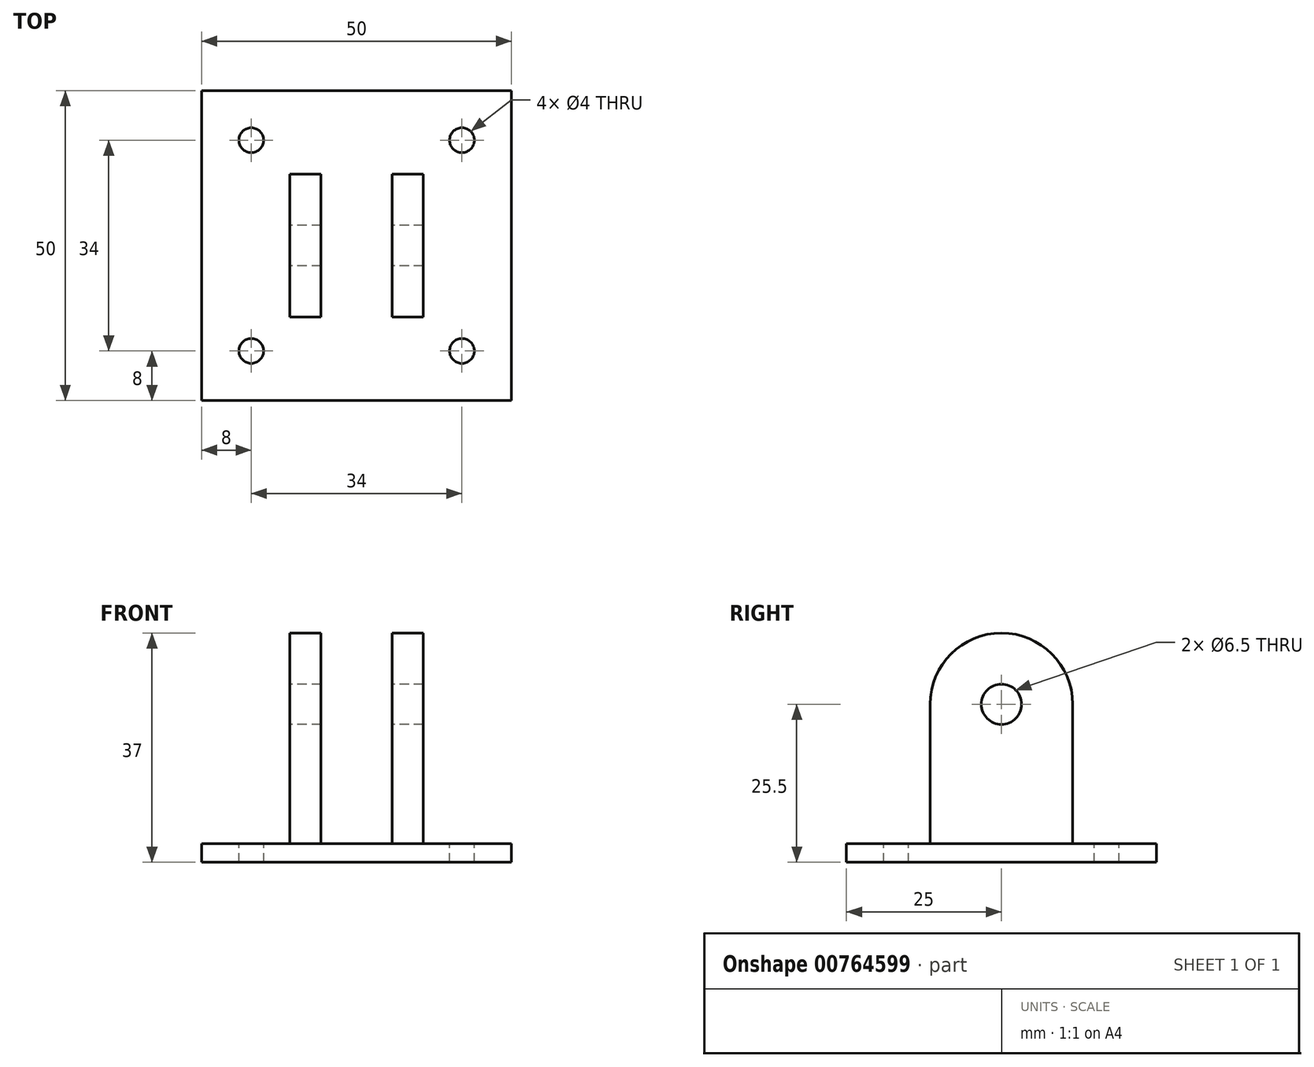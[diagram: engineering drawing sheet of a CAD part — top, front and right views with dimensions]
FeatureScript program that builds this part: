
annotation { "Feature Type Name" : "Feature", "Feature Type Description" : "" }
export const myFeature = defineFeature(function(context is Context, id is Id, definition is map)
    precondition{}
    {
        {
            var Q0;
            Q0=qCreatedBy(makeId("Top.planeOp"),FACE);
            var sketch = newSketch(context, id + "F0", { "sketchPlane" : qUnion([Q0])});
            skLineSegment(sketch, "E0.bottom", {"start": v(-25, 25) * mm, "end": v(25, 25) * mm});
            skLineSegment(sketch, "E0.top", {"start": v(-25, -25) * mm, "end": v(25, -25) * mm});
            skLineSegment(sketch, "E0.left", {"start": v(-25, 25) * mm, "end": v(-25, -25) * mm});
            skLineSegment(sketch, "E0.right", {"start": v(25, 25) * mm, "end": v(25, -25) * mm});
            skPoint(sketch, "E0.middle", {"position": v(0, 0) * mm});
            skSolve(sketch);
        }
        {
            var Q0;
            Q0=makeQuery(id+"F0.imprint","IMPRINT",FACE,{"disambiguationData":[TD([[makeQuery(id+"F0.imprint","IMPRINT",EDGE,{"derivedFrom":sQuery(id+"F0.wireOp",EDGE,"E0.bottom")}),-1.0]])]});
            extrude(context, id + "F1", {"entities" : qUnion([Q0]), "depth" : 3 * mm, "offsetDistance" : 25 * mm});
        }
        {
            var Q0;
            Q0=makeQuery(id+"F1.opExtrude","CAP_FACE",FACE,{"disambiguationData":[OSD([sQuery(id+"F0.wireOp",EDGE,"E0.bottom"),sQuery(id+"F0.wireOp",EDGE,"E0.top"),sQuery(id+"F0.wireOp",EDGE,"E0.left"),sQuery(id+"F0.wireOp",EDGE,"E0.right")])],"isStart":false});
            var sketch = newSketch(context, id + "F2", { "sketchPlane" : qUnion([Q0])});
            skLineSegment(sketch, "E1", {"start": v(0, 25) * mm, "end": v(0, -25) * mm});
            skLineSegment(sketch, "E2", {"start": v(0, -25) * mm, "end": v(0, 0) * mm});
            skLineSegment(sketch, "E3", {"start": v(0, 0) * mm, "end": v(-5.75, 0) * mm});
            skLineSegment(sketch, "E4", {"start": v(-5.75, 0) * mm, "end": v(5.75, 0) * mm});
            skLineSegment(sketch, "E5", {"start": v(-10.75, 0) * mm, "end": v(-10.75, 11.5) * mm});
            skLineSegment(sketch, "E6", {"start": v(-5.75, 11.5) * mm, "end": v(-5.75, 0) * mm});
            skLineSegment(sketch, "E7", {"start": v(-5.75, 0) * mm, "end": v(-5.75, -11.5) * mm});
            skLineSegment(sketch, "E8", {"start": v(-10.75, -11.5) * mm, "end": v(-10.75, 0) * mm});
            skLineSegment(sketch, "E9", {"start": v(5.75, 0) * mm, "end": v(5.75, 11.5) * mm});
            skLineSegment(sketch, "E10", {"start": v(10.75, 11.5) * mm, "end": v(10.75, 0) * mm});
            skLineSegment(sketch, "E11", {"start": v(10.75, 0) * mm, "end": v(10.75, -11.5) * mm});
            skLineSegment(sketch, "E12", {"start": v(5.75, -11.5) * mm, "end": v(5.75, 0) * mm});
            skLineSegment(sketch, "E13", {"start": v(-10.75, 11.5) * mm, "end": v(-5.75, 11.5) * mm});
            skLineSegment(sketch, "E14", {"start": v(-5.75, -11.5) * mm, "end": v(-10.75, -11.5) * mm});
            skLineSegment(sketch, "E15", {"start": v(5.75, -11.5) * mm, "end": v(10.75, -11.5) * mm});
            skLineSegment(sketch, "E16", {"start": v(10.75, 11.5) * mm, "end": v(5.75, 11.5) * mm});
            skLineSegment(sketch, "E17", {"start": v(25, -20) * mm, "end": v(25, -25) * mm});
            skLineSegment(sketch, "E18", {"start": v(25, -25) * mm, "end": v(20, -20) * mm});
            skLineSegment(sketch, "E19", {"start": v(-25, -25) * mm, "end": v(-20, -20) * mm});
            skLineSegment(sketch, "E20", {"start": v(-25, 25) * mm, "end": v(-20, 20) * mm});
            skLineSegment(sketch, "E21", {"start": v(25, 25) * mm, "end": v(20, 20) * mm});
            skPoint(sketch, "E22", {"position": v(-20, 20) * mm});
            skPoint(sketch, "E23", {"position": v(20, 20) * mm});
            skPoint(sketch, "E24", {"position": v(20, -20) * mm});
            skPoint(sketch, "E25", {"position": v(-20, -20) * mm});
            skCircle(sketch, "E26", {"center": v(-20, 20) * mm, "radius": 3.25 * mm});
            skCircle(sketch, "E27", {"center": v(20, 20) * mm, "radius": 3.25 * mm});
            skCircle(sketch, "E28", {"center": v(20, -20) * mm, "radius": 3.25 * mm});
            skCircle(sketch, "E29", {"center": v(-20, -20) * mm, "radius": 3.25 * mm});
            skSolve(sketch);
        }
        {
            var Q0;
            Q0=makeQuery(id+"F2.imprint","IMPRINT",FACE,{"disambiguationData":[TD([[makeQuery(id+"F2.imprint","IMPRINT",EDGE,{"derivedFrom":sQuery(id+"F2.wireOp",EDGE,"E9")}),-1.0]])]});
            var Q1;
            Q1=makeQuery(id+"F2.imprint","IMPRINT",FACE,{"disambiguationData":[TD([[makeQuery(id+"F2.imprint","IMPRINT",EDGE,{"derivedFrom":sQuery(id+"F2.wireOp",EDGE,"E5")}),-1.0]])]});
            extrude(context, id + "F3", {"entities" : qUnion([Q0, Q1]), "operationType" : NewBodyOperationType.ADD, "depth" : (24 + 10) * mm, "offsetDistance" : 25 * mm});
        }
        {
            var Q0;
            Q0=makeQuery(id+"F3.opExtrude","CAP_EDGE",EDGE,{"disambiguationData":[OSD([sQuery(id+"F2.wireOp",EDGE,"E14")])],"isStart":false});
            var Q1;
            Q1=makeQuery(id+"F3.opExtrude","CAP_EDGE",EDGE,{"disambiguationData":[OSD([sQuery(id+"F2.wireOp",EDGE,"E15")])],"isStart":false});
            var Q2;
            Q2=makeQuery(id+"F3.opExtrude","CAP_EDGE",EDGE,{"disambiguationData":[OSD([sQuery(id+"F2.wireOp",EDGE,"E16")])],"isStart":false});
            var Q3;
            Q3=makeQuery(id+"F3.opExtrude","CAP_EDGE",EDGE,{"disambiguationData":[OSD([sQuery(id+"F2.wireOp",EDGE,"E13")])],"isStart":false});
            fillet(context, id + "F4", {"entities" : qUnion([Q0, Q1, Q2, Q3]), "radius" : 11.5 * mm, "tangentPropagation" : true, "allowEdgeOverflow" : false});
        }
        {
            var Q0;
            Q0=makeQuery(id+"F3.opExtrude","SWEPT_FACE",FACE,{"disambiguationData":[OSD([sQuery(id+"F2.wireOp",EDGE,"E5"),sQuery(id+"F2.wireOp",EDGE,"E8")])]});
            var sketch = newSketch(context, id + "F5", { "sketchPlane" : qUnion([Q0])});
            skPoint(sketch, "E30", {"position": v(11.5, 25.5) * mm});
            skPoint(sketch, "E31", {"position": v(0, 25.5) * mm});
            skSolve(sketch);
        }
        {
            var Q0;
            Q0=sQuery(id+"F5.wireOp",VERTEX,"E31");
            var Q1;
            Q1=makeQuery(id+"F1.opExtrude","SWEPT_BODY",BODY,{"disambiguationData":[OSD([sQuery(id+"F0.wireOp",EDGE,"E0.bottom"),sQuery(id+"F0.wireOp",EDGE,"E0.top"),sQuery(id+"F0.wireOp",EDGE,"E0.left"),sQuery(id+"F0.wireOp",EDGE,"E0.right")])]});
            hole(context, id + "F6", {"style" : HoleStyle.SIMPLE, "endStyle" : HoleEndStyle.THROUGH, "holeDiameter" : 6.5 * mm, "majorDiameter" : 5 * mm, "isTappedThrough" : true, "tappedDepth" : 12 * mm, "tapClearance" : 3, "locations" : qUnion([Q0]), "scope" : qUnion([Q1])});
        }
        {
            var Q0;
            Q0=makeQuery(id+"F1.opExtrude","CAP_FACE",FACE,{"disambiguationData":[OSD([sQuery(id+"F0.wireOp",EDGE,"E0.bottom"),sQuery(id+"F0.wireOp",EDGE,"E0.top"),sQuery(id+"F0.wireOp",EDGE,"E0.left"),sQuery(id+"F0.wireOp",EDGE,"E0.right")])],"isStart":false});
            var sketch = newSketch(context, id + "F7", { "sketchPlane" : qUnion([Q0])});
            skPoint(sketch, "E32", {"position": v(-17, 17) * mm});
            skPoint(sketch, "E33", {"position": v(17, 17) * mm});
            skPoint(sketch, "E34", {"position": v(17, -17) * mm});
            skPoint(sketch, "E35", {"position": v(-17, -17) * mm});
            skSolve(sketch);
        }
        {
            var Q0;
            Q0=sQuery(id+"F7.wireOp",VERTEX,"E32");
            var Q1;
            Q1=sQuery(id+"F7.wireOp",VERTEX,"E33");
            var Q2;
            Q2=sQuery(id+"F7.wireOp",VERTEX,"E34");
            var Q3;
            Q3=sQuery(id+"F7.wireOp",VERTEX,"E35");
            var Q4;
            Q4=makeQuery(id+"F1.opExtrude","SWEPT_BODY",BODY,{"disambiguationData":[OSD([sQuery(id+"F0.wireOp",EDGE,"E0.bottom"),sQuery(id+"F0.wireOp",EDGE,"E0.top"),sQuery(id+"F0.wireOp",EDGE,"E0.left"),sQuery(id+"F0.wireOp",EDGE,"E0.right")])]});
            hole(context, id + "F8", {"style" : HoleStyle.SIMPLE, "endStyle" : HoleEndStyle.BLIND, "holeDiameter" : 4 * mm, "majorDiameter" : 5 * mm, "holeDepth" : 15 * mm, "isTappedThrough" : true, "tappedDepth" : 12 * mm, "tapClearance" : 3, "locations" : qUnion([Q0, Q1, Q2, Q3]), "scope" : qUnion([Q4])});
        }
    });
